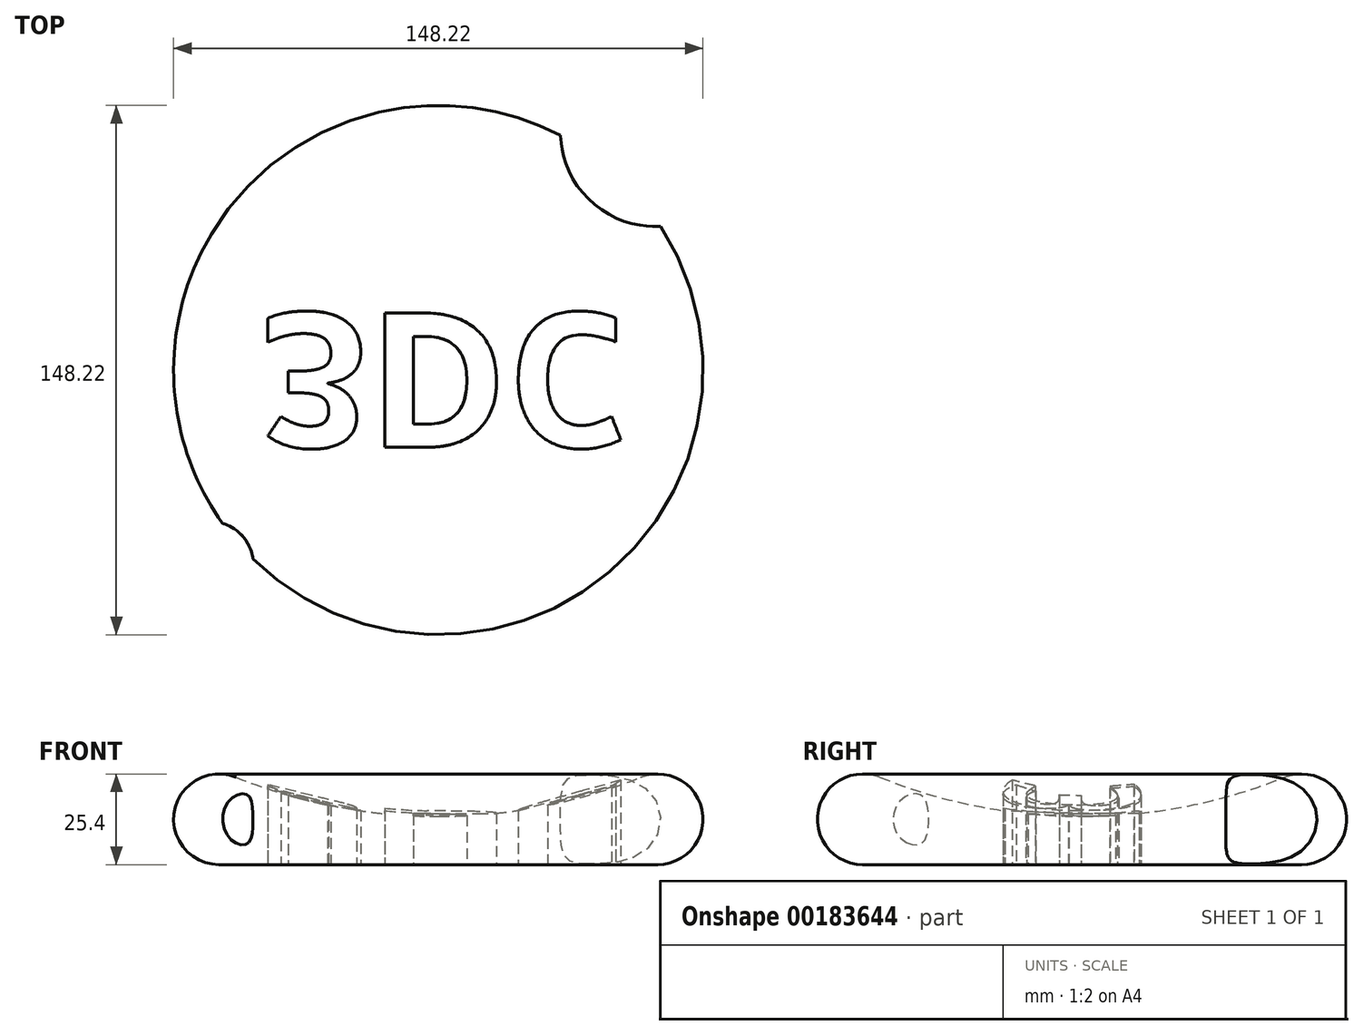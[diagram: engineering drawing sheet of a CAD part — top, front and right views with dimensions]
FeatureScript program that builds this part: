
annotation { "Feature Type Name" : "Feature", "Feature Type Description" : "" }
export const myFeature = defineFeature(function(context is Context, id is Id, definition is map)
    precondition{}
    {
        {
            var Q0;
            Q0=qCreatedBy(makeId("Front.planeOp"),FACE);
            var sketch = newSketch(context, id + "F0", { "sketchPlane" : qUnion([Q0])});
            skArc(sketch, "E0", {"start": v(-56.67, 24.48) * mm, "mid": v(-73.88, 15.11) * mm, "end": v(-61.41, 0) * mm});
            skLineSegment(sketch, "E1", {"start": v(0, 0) * mm, "end": v(-61.41, 0) * mm});
            skPoint(sketch, "E2.center.orphan", {"position": v(0, 165.4) * mm});
            skArc(sketch, "E3", {"start": v(-56.67, 24.48) * mm, "mid": v(-28.86, 16.28) * mm, "end": v(0, 13.51) * mm});
            skLineSegment(sketch, "E4", {"start": v(0, 0) * mm, "end": v(0, 13.51) * mm});
            skSolve(sketch);
        }
        {
            var Q0;
            Q0=makeQuery(id+"F0.imprint","IMPRINT",FACE,{"disambiguationData":[TD([[makeQuery(id+"F0.imprint","IMPRINT",EDGE,{"derivedFrom":sQuery(id+"F0.wireOp",EDGE,"E0")}),1.0]])]});
            var sketch = newSketch(context, id + "F1", { "sketchPlane" : qUnion([Q0])});
            skArc(sketch, "E5.0.0", {"start": v(0, 13.51) * mm, "mid": v(-28.86, 16.28) * mm, "end": v(-56.67, 24.48) * mm});
            skArc(sketch, "E5.0.1", {"start": v(-56.67, 24.48) * mm, "mid": v(-73.88, 15.11) * mm, "end": v(-61.41, 0) * mm});
            skLineSegment(sketch, "E5.0.2", {"start": v(-61.41, 0) * mm, "end": v(0, 0) * mm});
            skLineSegment(sketch, "E5.0.3", {"start": v(0, 0) * mm, "end": v(0, 13.51) * mm});
            skSolve(sketch);
        }
        {
            var Q0;
            Q0=makeQuery(id+"F0.imprint","IMPRINT",FACE,{"disambiguationData":[TD([[makeQuery(id+"F0.imprint","IMPRINT",EDGE,{"derivedFrom":sQuery(id+"F0.wireOp",EDGE,"E0")}),1.0]])]});
            var Q1;
            Q1=sQuery(id+"F1.wireOp",EDGE,"E5.0.3");
            revolve(context, id + "F2", {"entities" : qUnion([Q0]), "axis" : qUnion([Q1]), "revolveType" : RevolveType.FULL});
        }
        {
            var Q0;
            Q0=makeQuery(id+"F2.opRevolve","SWEPT_FACE",FACE,{"disambiguationData":[OSD([sQuery(id+"F0.wireOp",EDGE,"E1")])]});
            var sketch = newSketch(context, id + "F3", { "sketchPlane" : qUnion([Q0])});
            skCircle(sketch, "E6", {"center": v(-63.8, 54.44) * mm, "radius": 12 * mm});
            skText(sketch, "E7", { "text": "3DC", "fontName": "OpenSans-Bold.ttf"});
            const initialGuessF3  = {"E7": [-0.0498, -0.01603, 1, 0, 0.03797]};
            skSetInitialGuess(sketch, initialGuessF3);
            skSolve(sketch);
        }
        {
            var Q0;
            Q0 = qSketchRegion(id + "F3", true);
            extrude(context, id + "F4", {"entities" : qUnion([Q0]), "operationType" : NewBodyOperationType.REMOVE, "oppositeDirection" : true, "depth" : 33.53 * mm});
        }
        {
            var Q0;
            Q0=qCreatedBy(makeId("Top.planeOp"),FACE);
            var sketch = newSketch(context, id + "F5", { "sketchPlane" : qUnion([Q0])});
            skCircle(sketch, "E8", {"center": v(60.7, 66.8) * mm, "radius": 26.55 * mm});
            skSolve(sketch);
        }
        {
            var Q0;
            Q0 = qSketchRegion(id + "F5", true);
            extrude(context, id + "F6", {"entities" : qUnion([Q0]), "operationType" : NewBodyOperationType.REMOVE, "depth" : 66.3 * mm});
        }
    });
